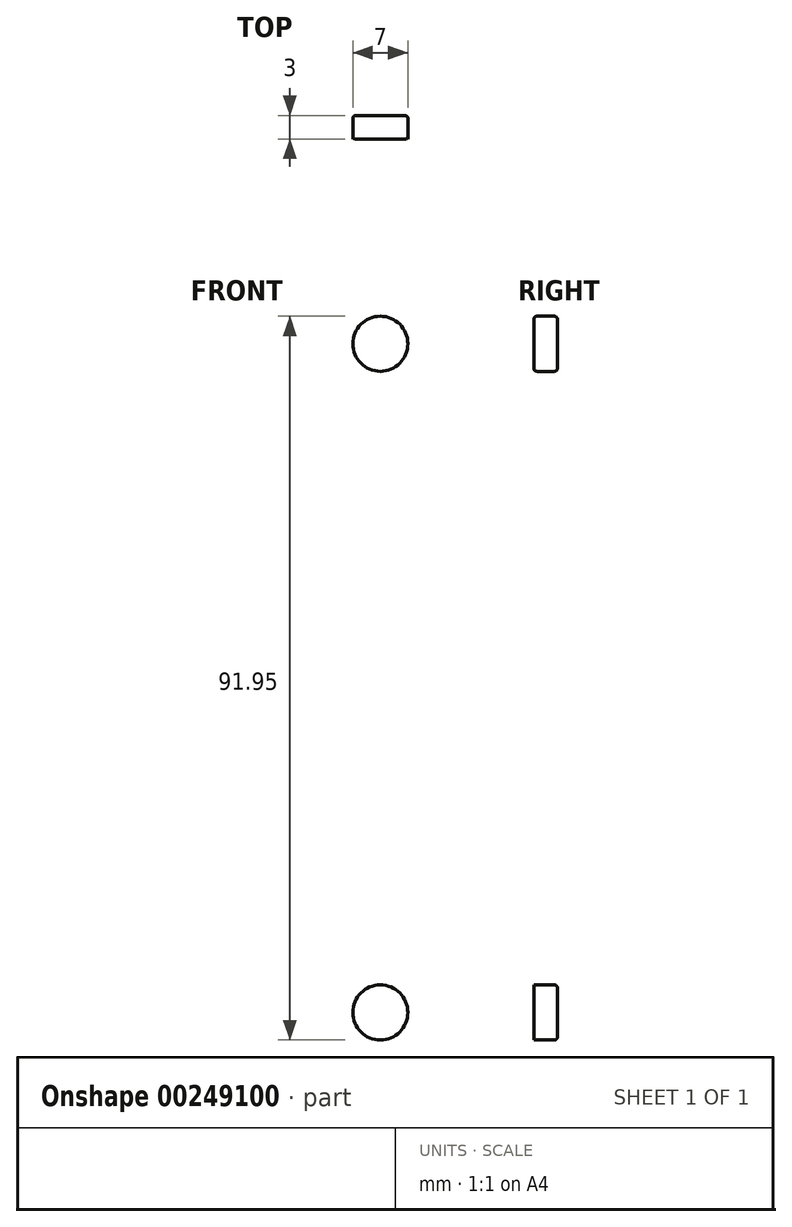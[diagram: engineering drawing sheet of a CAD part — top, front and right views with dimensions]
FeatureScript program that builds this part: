
annotation { "Feature Type Name" : "Feature", "Feature Type Description" : "" }
export const myFeature = defineFeature(function(context is Context, id is Id, definition is map)
    precondition{}
    {
        {
            var Q0;
            Q0=qCreatedBy(makeId("Top.planeOp"),FACE);
            var sketch = newSketch(context, id + "F0", { "sketchPlane" : qUnion([Q0])});
            skLineSegment(sketch, "E0.bottom", {"start": v(63, 1.5) * mm, "end": v(-63, 1.5) * mm});
            skLineSegment(sketch, "E0.top", {"start": v(63, -1.5) * mm, "end": v(-63, -1.5) * mm});
            skLineSegment(sketch, "E0.left", {"start": v(63, 1.5) * mm, "end": v(63, -1.5) * mm});
            skLineSegment(sketch, "E0.right", {"start": v(-63, 1.5) * mm, "end": v(-63, -1.5) * mm});
            skPoint(sketch, "E0.middle", {"position": v(0, 0) * mm});
            skSolve(sketch);
        }
        {
            var Q0;
            Q0=makeQuery(id+"F0.imprint","IMPRINT",FACE,{"disambiguationData":[TD([[makeQuery(id+"F0.imprint","IMPRINT",EDGE,{"derivedFrom":sQuery(id+"F0.wireOp",EDGE,"E0.bottom")}),1.0]])]});
            extrude(context, id + "F1", {"entities" : qUnion([Q0]), "depth" : 98.75 * mm});
        }
        {
            var Q0;
            Q0=makeQuery(id+"F1.opExtrude","SWEPT_FACE",FACE,{"disambiguationData":[OSD([sQuery(id+"F0.wireOp",EDGE,"E0.top")])]});
            var sketch = newSketch(context, id + "F2", { "sketchPlane" : qUnion([Q0])});
            skCircle(sketch, "E1", {"center": v(-54.02, 91.85) * mm, "radius": 3.5 * mm});
            skCircle(sketch, "E2", {"center": v(-54.02, 6.9) * mm, "radius": 3.5 * mm});
            skLineSegment(sketch, "E3", {"start": v(0, 79.59) * mm, "end": v(0, 45.8) * mm});
            skCircle(sketch, "E4.MirrorC", {"center": v(54.02, 91.85) * mm, "radius": 3.5 * mm});
            skCircle(sketch, "E5.MirrorC", {"center": v(54.02, 6.9) * mm, "radius": 3.5 * mm});
            skCircle(sketch, "E6", {"center": v(0, 98.75) * mm, "radius": 4.5 * mm});
            skSolve(sketch);
        }
        {
            var Q0;
            Q0=makeQuery(id+"F2.imprint","IMPRINT",FACE,{"disambiguationData":[TD([[makeQuery(id+"F2.imprint","IMPRINT",EDGE,{"derivedFrom":sQuery(id+"F2.wireOp",EDGE,"E1")}),1.0]])]});
            var Q1;
            {var subQ0=sQuery(id+"F2.wireOp",EDGE,"E6");var subQ1=makeQuery(id+"F1.opExtrude","CAP_EDGE",EDGE,{"disambiguationData":[OSD([sQuery(id+"F0.wireOp",EDGE,"E0.top")])],"isStart":false});var subQ2=makeQuery(id+"F2.imprint","INTERSECT",VERTEX,{"disambiguationData":[OD(0.0)],"derivedFrom":[subQ1,subQ0]});Q1=makeQuery(id+"F2.imprint","IMPRINT",FACE,{"disambiguationData":[TD([[makeQuery(id+"F2.imprint","IMPRINT",EDGE,{"disambiguationData":[TD([[subQ2,1.0]])],"derivedFrom":subQ0}),1.0]])]});}
            var Q2;
            Q2=makeQuery(id+"F2.imprint","IMPRINT",FACE,{"disambiguationData":[TD([[makeQuery(id+"F2.imprint","IMPRINT",EDGE,{"derivedFrom":sQuery(id+"F2.wireOp",EDGE,"E4.MirrorC")}),-1.0]])]});
            var Q3;
            Q3=makeQuery(id+"F2.imprint","IMPRINT",FACE,{"disambiguationData":[TD([[makeQuery(id+"F2.imprint","IMPRINT",EDGE,{"derivedFrom":sQuery(id+"F2.wireOp",EDGE,"E5.MirrorC")}),-1.0]])]});
            var Q4;
            Q4=makeQuery(id+"F2.imprint","IMPRINT",FACE,{"disambiguationData":[TD([[makeQuery(id+"F2.imprint","IMPRINT",EDGE,{"derivedFrom":sQuery(id+"F2.wireOp",EDGE,"E2")}),1.0]])]});
            extrude(context, id + "F3", {"entities" : qUnion([Q0, Q1, Q2, Q3, Q4]), "operationType" : NewBodyOperationType.REMOVE, "oppositeDirection" : true, "depth" : 25 * mm});
        }
        {
            var Q0;
            Q0=makeQuery(id+"F1.opExtrude","SWEPT_EDGE",EDGE,{"disambiguationData":[OSD([sQuery(id+"F0.wireOp",EDGE,"E0.bottom"),sQuery(id+"F0.wireOp",EDGE,"E0.left")])]});
            var Q1;
            Q1=makeQuery(id+"F1.opExtrude","SWEPT_EDGE",EDGE,{"disambiguationData":[OSD([sQuery(id+"F0.wireOp",EDGE,"E0.top"),sQuery(id+"F0.wireOp",EDGE,"E0.left")])]});
            var Q2;
            {var subQ0=sQuery(id+"F0.wireOp",EDGE,"E0.left");var subQ1=sQuery(id+"F0.wireOp",EDGE,"E0.top");Q2=makeQuery(id+"F3.boolean.opBoolean","SPLIT",EDGE,{"disambiguationData":[TD([makeQuery(id+"F1.opExtrude","SWEPT_FACE",FACE,{"disambiguationData":[OSD([subQ0])]})])],"derivedFrom":makeQuery(id+"F1.opExtrude","CAP_EDGE",EDGE,{"disambiguationData":[OSD([subQ1])],"isStart":false})});}
            var Q3;
            {var subQ0=sQuery(id+"F0.wireOp",EDGE,"E0.bottom");var subQ1=sQuery(id+"F0.wireOp",EDGE,"E0.left");Q3=makeQuery(id+"F3.boolean.opBoolean","SPLIT",EDGE,{"disambiguationData":[TD([makeQuery(id+"F1.opExtrude","SWEPT_FACE",FACE,{"disambiguationData":[OSD([subQ1])]})])],"derivedFrom":makeQuery(id+"F1.opExtrude","CAP_EDGE",EDGE,{"disambiguationData":[OSD([subQ0])],"isStart":false})});}
            var Q4;
            {var subQ0=sQuery(id+"F0.wireOp",EDGE,"E0.bottom");var subQ1=sQuery(id+"F0.wireOp",EDGE,"E0.right");Q4=makeQuery(id+"F3.boolean.opBoolean","SPLIT",EDGE,{"disambiguationData":[TD([makeQuery(id+"F1.opExtrude","SWEPT_FACE",FACE,{"disambiguationData":[OSD([subQ1])]})])],"derivedFrom":makeQuery(id+"F1.opExtrude","CAP_EDGE",EDGE,{"disambiguationData":[OSD([subQ0])],"isStart":false})});}
            var Q5;
            {var subQ0=sQuery(id+"F0.wireOp",EDGE,"E0.right");var subQ1=sQuery(id+"F0.wireOp",EDGE,"E0.top");Q5=makeQuery(id+"F3.boolean.opBoolean","SPLIT",EDGE,{"disambiguationData":[TD([makeQuery(id+"F1.opExtrude","SWEPT_FACE",FACE,{"disambiguationData":[OSD([subQ0])]})])],"derivedFrom":makeQuery(id+"F1.opExtrude","CAP_EDGE",EDGE,{"disambiguationData":[OSD([subQ1])],"isStart":false})});}
            var Q6;
            Q6=makeQuery(id+"F1.opExtrude","SWEPT_EDGE",EDGE,{"disambiguationData":[OSD([sQuery(id+"F0.wireOp",EDGE,"E0.top"),sQuery(id+"F0.wireOp",EDGE,"E0.right")])]});
            var Q7;
            Q7=makeQuery(id+"F1.opExtrude","SWEPT_EDGE",EDGE,{"disambiguationData":[OSD([sQuery(id+"F0.wireOp",EDGE,"E0.bottom"),sQuery(id+"F0.wireOp",EDGE,"E0.right")])]});
            var Q8;
            Q8=makeQuery(id+"F3.boolean.opBoolean","INTERSECT",EDGE,{"derivedFrom":[makeQuery(id+"F1.opExtrude","SWEPT_FACE",FACE,{"disambiguationData":[OSD([sQuery(id+"F0.wireOp",EDGE,"E0.bottom")])]}),makeQuery(id+"F3.opExtrude","SWEPT_FACE",FACE,{"disambiguationData":[OSD([sQuery(id+"F2.wireOp",EDGE,"E4.MirrorC")])]})]});
            var Q9;
            Q9=makeQuery(id+"F3.boolean.opBoolean","COPY",EDGE,{"derivedFrom":makeQuery(id+"F3.opExtrude","CAP_EDGE",EDGE,{"disambiguationData":[OSD([sQuery(id+"F2.wireOp",EDGE,"E4.MirrorC")])],"isStart":true})});
            var Q10;
            Q10=makeQuery(id+"F3.boolean.opBoolean","INTERSECT",EDGE,{"derivedFrom":[makeQuery(id+"F1.opExtrude","SWEPT_FACE",FACE,{"disambiguationData":[OSD([sQuery(id+"F0.wireOp",EDGE,"E0.bottom")])]}),makeQuery(id+"F3.opExtrude","SWEPT_FACE",FACE,{"disambiguationData":[OSD([sQuery(id+"F2.wireOp",EDGE,"E5.MirrorC")])]})]});
            var Q11;
            Q11=makeQuery(id+"F3.boolean.opBoolean","COPY",EDGE,{"derivedFrom":makeQuery(id+"F3.opExtrude","CAP_EDGE",EDGE,{"disambiguationData":[OSD([sQuery(id+"F2.wireOp",EDGE,"E5.MirrorC")])],"isStart":true})});
            var Q12;
            Q12=makeQuery(id+"F3.boolean.opBoolean","COPY",EDGE,{"derivedFrom":makeQuery(id+"F3.opExtrude","CAP_EDGE",EDGE,{"disambiguationData":[OSD([sQuery(id+"F2.wireOp",EDGE,"E2")])],"isStart":true})});
            var Q13;
            Q13=makeQuery(id+"F3.boolean.opBoolean","INTERSECT",EDGE,{"derivedFrom":[makeQuery(id+"F1.opExtrude","SWEPT_FACE",FACE,{"disambiguationData":[OSD([sQuery(id+"F0.wireOp",EDGE,"E0.bottom")])]}),makeQuery(id+"F3.opExtrude","SWEPT_FACE",FACE,{"disambiguationData":[OSD([sQuery(id+"F2.wireOp",EDGE,"E2")])]})]});
            var Q14;
            Q14=makeQuery(id+"F3.boolean.opBoolean","INTERSECT",EDGE,{"derivedFrom":[makeQuery(id+"F1.opExtrude","SWEPT_FACE",FACE,{"disambiguationData":[OSD([sQuery(id+"F0.wireOp",EDGE,"E0.bottom")])]}),makeQuery(id+"F3.opExtrude","SWEPT_FACE",FACE,{"disambiguationData":[OSD([sQuery(id+"F2.wireOp",EDGE,"E1")])]})]});
            var Q15;
            Q15=makeQuery(id+"F3.boolean.opBoolean","COPY",EDGE,{"derivedFrom":makeQuery(id+"F3.opExtrude","CAP_EDGE",EDGE,{"disambiguationData":[OSD([sQuery(id+"F2.wireOp",EDGE,"E1")])],"isStart":true})});
            var Q16;
            Q16=makeQuery(id+"F3.boolean.opBoolean","INTERSECT",EDGE,{"derivedFrom":[makeQuery(id+"F1.opExtrude","SWEPT_FACE",FACE,{"disambiguationData":[OSD([sQuery(id+"F0.wireOp",EDGE,"E0.bottom")])]}),makeQuery(id+"F3.opExtrude","SWEPT_FACE",FACE,{"disambiguationData":[OSD([sQuery(id+"F2.wireOp",EDGE,"E6")])]})]});
            var Q17;
            Q17=makeQuery(id+"F3.boolean.opBoolean","COPY",EDGE,{"derivedFrom":makeQuery(id+"F3.opExtrude","CAP_EDGE",EDGE,{"disambiguationData":[OSD([sQuery(id+"F2.wireOp",EDGE,"E6")])],"isStart":true})});
            fillet(context, id + "F4", {"entities" : qUnion([Q0, Q1, Q2, Q3, Q4, Q5, Q6, Q7, Q8, Q9, Q10, Q11, Q12, Q13, Q14, Q15, Q16, Q17]), "radius" : 0.4 * mm, "tangentPropagation" : true, "allowEdgeOverflow" : false});
        }
    });
